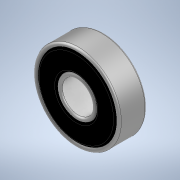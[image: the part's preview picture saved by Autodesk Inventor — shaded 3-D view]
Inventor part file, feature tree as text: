
AUTODESK INVENTOR PART (.ipt)
format: ipt  version: 2021 (Build 250183000, 183)  size: 209,408 bytes
history: native  units: mm
features: extrude x3, fillet x3, sketch x1
ambient origin geometry x8: Origin, YZ Plane, XZ Plane, XY Plane, X Axis, Y Axis, Z Axis, Center Point
bodies: Solid1 (feature_tree)
feature tree (7):
  sketch  "Sketch1"  dims[d0=8.0mm d1=22.0mm d2=10.0mm d3=20.0mm d4=7.0mm d5=0.0mm d6=0.5mm d8=7.0mm d9=0.0mm d10=0.5mm d11=7.0mm d12=0.0mm d13=0.5mm]
  extrude  "Extrusion1"  Depth=0.5mm
  fillet  "Fillet1"  Radius=10.0mm
  extrude  "Extrusion2"  Depth=0.5mm
  fillet  "Fillet3"  Radius=7.0mm
  extrude  "Extrusion3"  Depth=0.5mm
  fillet  "Fillet4"  Radius=7.0mm
